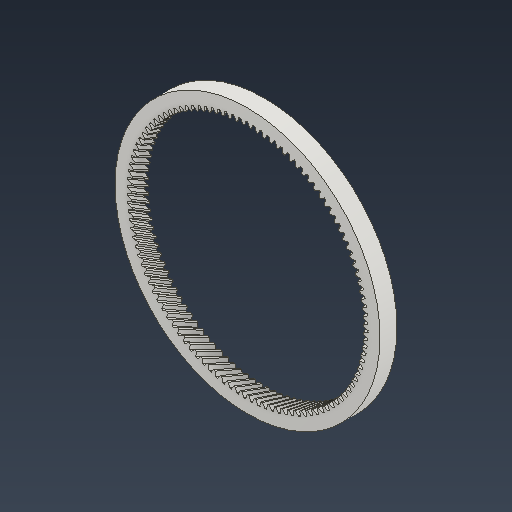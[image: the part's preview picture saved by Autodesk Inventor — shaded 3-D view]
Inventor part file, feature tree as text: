
AUTODESK INVENTOR PART (.ipt)
format: ipt  version: 2022 (Build 260153000, 153)  size: 1,352,704 bytes
history: native  units: mm (DEFAULTED — no unit token found)
features: plane x3, other x3, sketch x2, extrude x1
ambient origin geometry x8: Origin, YZ Plane, XZ Plane, XY Plane, X Axis, Y Axis, Z Axis, Center Point
bodies: Solid1 (feature_tree)
feature tree (9):
  extrude  "Extrusion1"  Depth=20.0mm TaperAngle=0.0deg
  plane  "Work Plane2"
  plane  "Work Plane8"
  plane  "Work Plane9"
  other  "Spur Gear"
  sketch  "Sketch1"  dims[d0=312.150718mm d1=20.0mm d2=0.0mm]
  sketch  "Sketch2"  dims[d3=277.994155mm d4=10.0mm d5=0.0mm d16=104.0mm d17=0.0mm d34=0.293607mm d39=0.0mm d45=0.0mm d47=104.0mm d50=0.0mm d51=0.0mm d52=104.0mm]
  other  "Srf1"
  other  "Pitch Diameter"
